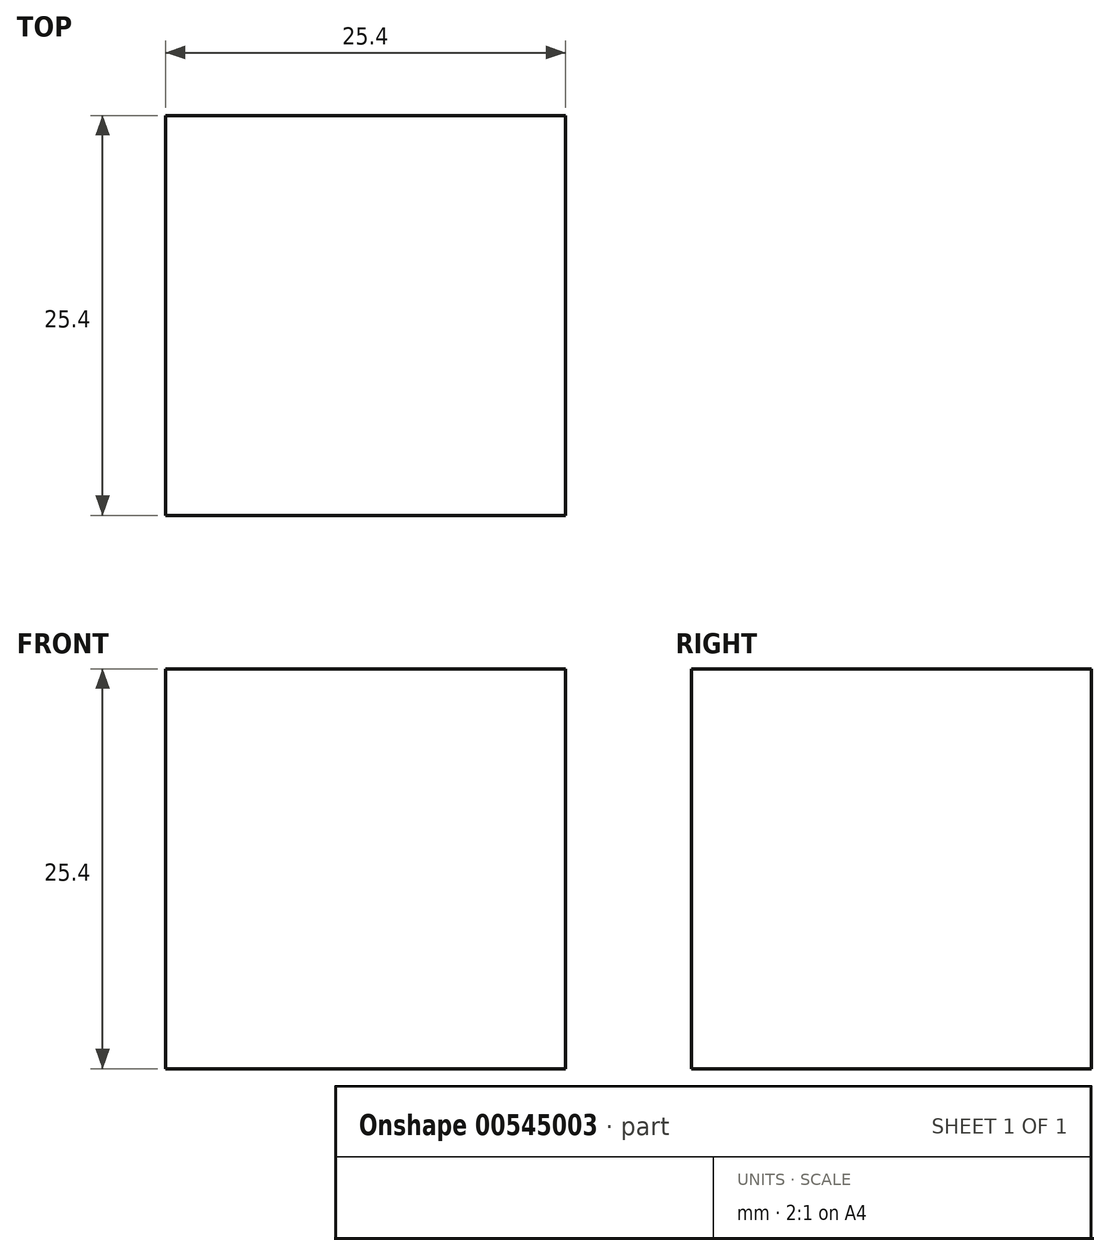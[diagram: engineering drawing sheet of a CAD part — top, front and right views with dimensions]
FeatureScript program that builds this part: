
annotation { "Feature Type Name" : "Feature", "Feature Type Description" : "" }
export const myFeature = defineFeature(function(context is Context, id is Id, definition is map)
    precondition{}
    {
        {
            var Q0;
            Q0=qCreatedBy(makeId("Top.planeOp"),FACE);
            var sketch = newSketch(context, id + "F0", { "sketchPlane" : qUnion([Q0])});
            skLineSegment(sketch, "E0.bottom", {"start": v(-12.7, -12.7) * mm, "end": v(12.7, -12.7) * mm});
            skLineSegment(sketch, "E0.top", {"start": v(-12.7, 12.7) * mm, "end": v(12.7, 12.7) * mm});
            skLineSegment(sketch, "E0.left", {"start": v(-12.7, -12.7) * mm, "end": v(-12.7, 12.7) * mm});
            skLineSegment(sketch, "E0.right", {"start": v(12.7, -12.7) * mm, "end": v(12.7, 12.7) * mm});
            skSolve(sketch);
        }
        {
            var Q0;
            Q0=makeQuery(id+"F0.imprint","IMPRINT",FACE,{"disambiguationData":[TD([[makeQuery(id+"F0.imprint","IMPRINT",EDGE,{"derivedFrom":sQuery(id+"F0.wireOp",EDGE,"E0.bottom")}),1.0]])]});
            extrude(context, id + "F1", {"entities" : qUnion([Q0]), "oppositeDirection" : true, "depth" : 25.4 * mm, "offsetDistance" : 25.4 * mm});
        }
    });
